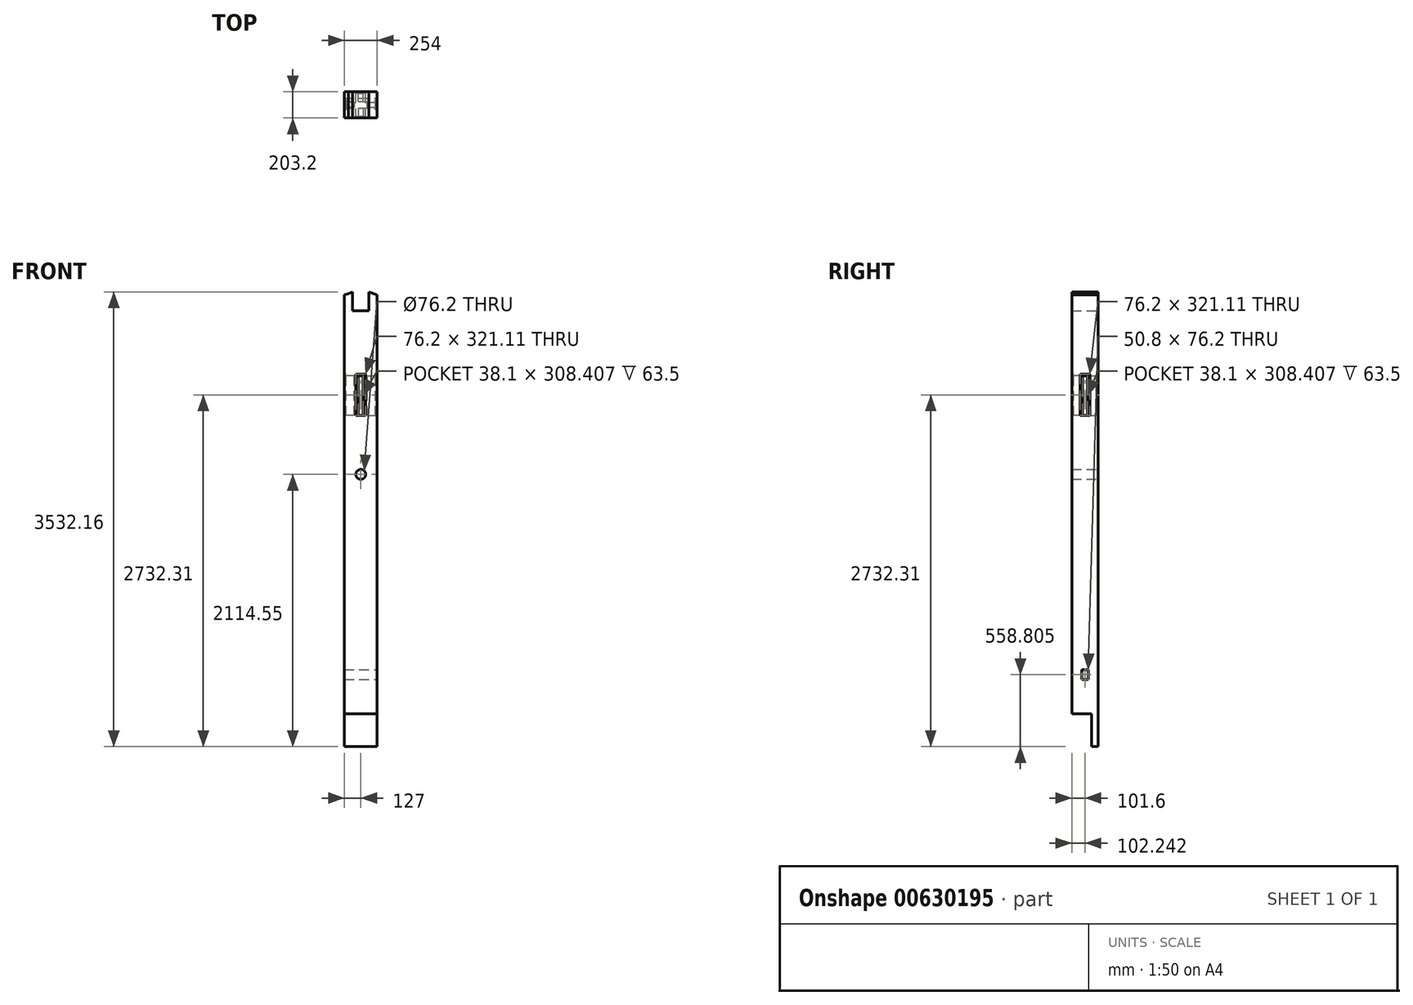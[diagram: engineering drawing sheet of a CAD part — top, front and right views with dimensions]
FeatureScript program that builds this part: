
annotation { "Feature Type Name" : "Feature", "Feature Type Description" : "" }
export const myFeature = defineFeature(function(context is Context, id is Id, definition is map)
    precondition{}
    {
        {
            var Q0;
            Q0=qCreatedBy(makeId("Front.planeOp"),FACE);
            var sketch = newSketch(context, id + "F0", { "sketchPlane" : qUnion([Q0])});
            skLineSegment(sketch, "E0.bottom", {"start": v(-127, 1679.58) * mm, "end": v(127, 1679.58) * mm});
            skLineSegment(sketch, "E0.top", {"start": v(-127, -1679.58) * mm, "end": v(127, -1679.58) * mm});
            skLineSegment(sketch, "E0.left", {"start": v(-127, 1679.58) * mm, "end": v(-127, -1679.58) * mm});
            skLineSegment(sketch, "E0.right", {"start": v(127, 1679.58) * mm, "end": v(127, -1679.57) * mm});
            skPoint(sketch, "E0.middle", {"position": v(0, 0) * mm});
            skLineSegment(sketch, "E1.bottom", {"start": v(-63.5, 1679.58) * mm, "end": v(63.5, 1679.58) * mm});
            skLineSegment(sketch, "E1.top", {"start": v(-63.5, 1450.98) * mm, "end": v(63.5, 1450.98) * mm});
            skLineSegment(sketch, "E1.left", {"start": v(-63.5, 1679.58) * mm, "end": v(-63.5, 1450.98) * mm});
            skLineSegment(sketch, "E1.right", {"start": v(63.5, 1679.58) * mm, "end": v(63.5, 1450.98) * mm});
            skPoint(sketch, "E1.middle", {"position": v(0, 1565.27) * mm});
            skLineSegment(sketch, "E2", {"start": v(-127, 1575.48) * mm, "end": v(-97.13, 1586.25) * mm});
            skLineSegment(sketch, "E3", {"start": v(-97.13, 1586.25) * mm, "end": v(-114.3, 1679.58) * mm});
            skLineSegment(sketch, "E4", {"start": v(-111.15, 1662.43) * mm, "end": v(-63.5, 1679.58) * mm});
            skLineSegment(sketch, "E5", {"start": v(127, 1575.96) * mm, "end": v(97.1, 1586.63) * mm});
            skLineSegment(sketch, "E6", {"start": v(97.1, 1586.63) * mm, "end": v(114.3, 1679.58) * mm});
            skLineSegment(sketch, "E7", {"start": v(111.16, 1662.6) * mm, "end": v(63.5, 1679.58) * mm});
            skLineSegment(sketch, "E8.bottom", {"start": v(-19.05, 946.58) * mm, "end": v(19.05, 946.58) * mm});
            skLineSegment(sketch, "E8.top", {"start": v(-19.05, 638.18) * mm, "end": v(19.05, 638.18) * mm});
            skLineSegment(sketch, "E8.left", {"start": v(-19.05, 946.58) * mm, "end": v(-19.05, 638.18) * mm});
            skLineSegment(sketch, "E8.right", {"start": v(19.05, 946.58) * mm, "end": v(19.05, 638.18) * mm});
            skPoint(sketch, "E8.middle", {"position": v(0, 792.38) * mm});
            skLineSegment(sketch, "E9.bottom", {"start": v(38.1, 638.18) * mm, "end": v(-38.1, 638.18) * mm});
            skLineSegment(sketch, "E9.top", {"start": v(38.1, 959.28) * mm, "end": v(-38.1, 959.28) * mm});
            skLineSegment(sketch, "E9.left", {"start": v(38.1, 638.18) * mm, "end": v(38.1, 959.28) * mm});
            skLineSegment(sketch, "E9.right", {"start": v(-38.1, 638.18) * mm, "end": v(-38.1, 959.28) * mm});
            skLineSegment(sketch, "E10", {"start": v(-127, 1575.48) * mm, "end": v(-63.5, 1598.5) * mm});
            skLineSegment(sketch, "E11", {"start": v(127, 1575.96) * mm, "end": v(63.5, 1598.58) * mm});
            skCircle(sketch, "E12", {"center": v(0, 180.97) * mm, "radius": 38.1 * mm});
            skSolve(sketch);
        }
        {
            var Q0;
            Q0=makeQuery(id+"F0.imprint","IMPRINT",FACE,{"disambiguationData":[TD([[makeQuery(id+"F0.imprint","IMPRINT",EDGE,{"derivedFrom":sQuery(id+"F0.wireOp",EDGE,"ph5wAFCl-OnS3-WXPz-KjN0-k0vqOy9yEcDQ.bottom")}),-1.0]])]});
            var Q1;
            Q1=makeQuery(id+"F0.imprint","IMPRINT",FACE,{"disambiguationData":[TD([[makeQuery(id+"F0.imprint","IMPRINT",EDGE,{"derivedFrom":sQuery(id+"F0.wireOp",EDGE,"E1.top")}),-1.0]])]});
            var Q2;
            Q2=makeQuery(id+"F0.imprint","IMPRINT",FACE,{"disambiguationData":[TD([[makeQuery(id+"F0.imprint","IMPRINT",EDGE,{"derivedFrom":sQuery(id+"F0.wireOp",EDGE,"E8.bottom")}),-1.0]])]});
            var Q3;
            Q3=makeQuery(id+"F0.imprint","IMPRINT",FACE,{"disambiguationData":[TD([[makeQuery(id+"F0.imprint","IMPRINT",EDGE,{"derivedFrom":sQuery(id+"F0.wireOp",EDGE,"E8.bottom")}),1.0]])]});
            extrude(context, id + "F1", {"entities" : qUnion([Q0, Q1, Q2, Q3]), "depth" : 203.2 * mm, "offsetDistance" : 25.4 * mm});
        }
        {
            var Q0;
            Q0=makeQuery(id+"F0.imprint","IMPRINT",FACE,{"disambiguationData":[TD([[makeQuery(id+"F0.imprint","IMPRINT",EDGE,{"derivedFrom":sQuery(id+"F0.wireOp",EDGE,"E8.bottom")}),-1.0]])]});
            extrude(context, id + "F2", {"entities" : qUnion([Q0]), "operationType" : NewBodyOperationType.REMOVE, "depth" : 76.2 * mm, "offsetDistance" : 25.4 * mm});
        }
        {
            var Q0;
            Q0=makeQuery(id+"F1.opExtrude","CAP_FACE",FACE,{"disambiguationData":[OSD([sQuery(id+"F0.wireOp",EDGE,"E0.left"),sQuery(id+"F0.wireOp",EDGE,"E0.right"),sQuery(id+"F0.wireOp",EDGE,"E1.top"),sQuery(id+"F0.wireOp",EDGE,"E1.left"),sQuery(id+"F0.wireOp",EDGE,"E1.right"),sQuery(id+"F0.wireOp",EDGE,"E0.top"),sQuery(id+"F0.wireOp",EDGE,"ph5wAFCl-OnS3-WXPz-KjN0-k0vqOy9yEcDQ.top"),sQuery(id+"F0.wireOp",EDGE,"ph5wAFCl-OnS3-WXPz-KjN0-k0vqOy9yEcDQ.left"),sQuery(id+"F0.wireOp",EDGE,"ph5wAFCl-OnS3-WXPz-KjN0-k0vqOy9yEcDQ.right"),sQuery(id+"F0.wireOp",EDGE,"E2"),sQuery(id+"F0.wireOp",EDGE,"E3"),sQuery(id+"F0.wireOp",EDGE,"E4"),sQuery(id+"F0.wireOp",EDGE,"E5"),sQuery(id+"F0.wireOp",EDGE,"E6"),sQuery(id+"F0.wireOp",EDGE,"E7")])],"isStart":false});
            var sketch = newSketch(context, id + "F3", { "sketchPlane" : qUnion([Q0])});
            skLineSegment(sketch, "E13.bottom", {"start": v(-19.05, 638.18) * mm, "end": v(19.05, 638.18) * mm});
            skLineSegment(sketch, "E13.top", {"start": v(-19.05, 946.58) * mm, "end": v(19.05, 946.58) * mm});
            skLineSegment(sketch, "E13.left", {"start": v(-19.05, 638.18) * mm, "end": v(-19.05, 946.58) * mm});
            skLineSegment(sketch, "E13.right", {"start": v(19.05, 638.18) * mm, "end": v(19.05, 946.58) * mm});
            skPoint(sketch, "E13.middle", {"position": v(0, 792.38) * mm});
            skLineSegment(sketch, "E14.bottom", {"start": v(-38.1, 638.18) * mm, "end": v(38.1, 638.18) * mm});
            skLineSegment(sketch, "E14.top", {"start": v(-38.1, 959.28) * mm, "end": v(38.1, 959.28) * mm});
            skLineSegment(sketch, "E14.left", {"start": v(-38.1, 638.18) * mm, "end": v(-38.1, 959.28) * mm});
            skLineSegment(sketch, "E14.right", {"start": v(38.1, 638.18) * mm, "end": v(38.1, 959.28) * mm});
            skSolve(sketch);
        }
        {
            var Q0;
            Q0=makeQuery(id+"F3.imprint","IMPRINT",FACE,{"disambiguationData":[TD([[makeQuery(id+"F3.imprint","IMPRINT",EDGE,{"derivedFrom":sQuery(id+"F3.wireOp",EDGE,"E13.top")}),-1.0]])]});
            extrude(context, id + "F4", {"entities" : qUnion([Q0]), "operationType" : NewBodyOperationType.REMOVE, "oppositeDirection" : true, "depth" : 76.2 * mm, "offsetDistance" : 25.4 * mm});
        }
        {
            var Q0;
            Q0=makeQuery(id+"F3.imprint","IMPRINT",FACE,{"disambiguationData":[TD([[makeQuery(id+"F3.imprint","IMPRINT",EDGE,{"derivedFrom":sQuery(id+"F3.wireOp",EDGE,"E13.top")}),1.0]])]});
            extrude(context, id + "F5", {"entities" : qUnion([Q0]), "operationType" : NewBodyOperationType.REMOVE, "oppositeDirection" : true, "depth" : 12.7 * mm, "offsetDistance" : 25.4 * mm});
        }
        {
            var Q0;
            Q0=makeQuery(id+"F0.imprint","IMPRINT",FACE,{"disambiguationData":[TD([[makeQuery(id+"F0.imprint","IMPRINT",EDGE,{"derivedFrom":sQuery(id+"F0.wireOp",EDGE,"E8.bottom")}),1.0]])]});
            extrude(context, id + "F6", {"entities" : qUnion([Q0]), "operationType" : NewBodyOperationType.REMOVE, "depth" : 12.7 * mm, "offsetDistance" : 25.4 * mm});
        }
        {
            var Q0;
            Q0=makeQuery(id+"F1.opExtrude","SWEPT_FACE",FACE,{"disambiguationData":[OSD([sQuery(id+"F0.wireOp",EDGE,"E0.right")])]});
            var sketch = newSketch(context, id + "F7", { "sketchPlane" : qUnion([Q0])});
            skLineSegment(sketch, "E15.bottom", {"start": v(-120.65, 638.18) * mm, "end": v(-82.55, 638.18) * mm});
            skLineSegment(sketch, "E15.top", {"start": v(-120.65, 946.58) * mm, "end": v(-82.55, 946.58) * mm});
            skLineSegment(sketch, "E15.left", {"start": v(-120.65, 638.18) * mm, "end": v(-120.65, 946.58) * mm});
            skLineSegment(sketch, "E15.right", {"start": v(-82.55, 638.18) * mm, "end": v(-82.55, 946.58) * mm});
            skPoint(sketch, "E15.middle", {"position": v(-101.6, 792.38) * mm});
            skLineSegment(sketch, "E16.bottom", {"start": v(-139.7, 638.18) * mm, "end": v(-63.5, 638.18) * mm});
            skLineSegment(sketch, "E16.top", {"start": v(-139.7, 959.28) * mm, "end": v(-63.5, 959.28) * mm});
            skLineSegment(sketch, "E16.left", {"start": v(-139.7, 638.18) * mm, "end": v(-139.7, 959.28) * mm});
            skLineSegment(sketch, "E16.right", {"start": v(-63.5, 638.18) * mm, "end": v(-63.5, 959.28) * mm});
            skLineSegment(sketch, "E17.bottom", {"start": v(-126.36, -1336.67) * mm, "end": v(-75.56, -1336.67) * mm});
            skLineSegment(sketch, "E17.top", {"start": v(-126.36, -1412.87) * mm, "end": v(-75.56, -1412.87) * mm});
            skLineSegment(sketch, "E17.left", {"start": v(-126.36, -1336.67) * mm, "end": v(-126.36, -1412.87) * mm});
            skLineSegment(sketch, "E17.right", {"start": v(-75.56, -1336.67) * mm, "end": v(-75.56, -1412.87) * mm});
            skPoint(sketch, "E17.middle", {"position": v(-100.96, -1374.77) * mm});
            skSolve(sketch);
        }
        {
            var Q0;
            Q0=makeQuery(id+"F7.imprint","IMPRINT",FACE,{"disambiguationData":[TD([[makeQuery(id+"F7.imprint","IMPRINT",EDGE,{"derivedFrom":sQuery(id+"F7.wireOp",EDGE,"E15.top")}),-1.0]])]});
            extrude(context, id + "F8", {"entities" : qUnion([Q0]), "operationType" : NewBodyOperationType.REMOVE, "oppositeDirection" : true, "depth" : 76.2 * mm, "offsetDistance" : 25.4 * mm});
        }
        {
            var Q0;
            Q0=makeQuery(id+"F7.imprint","IMPRINT",FACE,{"disambiguationData":[TD([[makeQuery(id+"F7.imprint","IMPRINT",EDGE,{"derivedFrom":sQuery(id+"F7.wireOp",EDGE,"E15.top")}),1.0]])]});
            extrude(context, id + "F9", {"entities" : qUnion([Q0]), "operationType" : NewBodyOperationType.REMOVE, "oppositeDirection" : true, "depth" : 12.7 * mm, "offsetDistance" : 25.4 * mm});
        }
        {
            var Q0;
            Q0=makeQuery(id+"F1.opExtrude","SWEPT_FACE",FACE,{"disambiguationData":[OSD([sQuery(id+"F0.wireOp",EDGE,"E0.left")])]});
            var sketch = newSketch(context, id + "F10", { "sketchPlane" : qUnion([Q0])});
            skLineSegment(sketch, "E18.bottom", {"start": v(82.55, 638.18) * mm, "end": v(120.65, 638.18) * mm});
            skLineSegment(sketch, "E18.top", {"start": v(82.55, 946.58) * mm, "end": v(120.65, 946.58) * mm});
            skLineSegment(sketch, "E18.left", {"start": v(82.55, 638.18) * mm, "end": v(82.55, 946.58) * mm});
            skLineSegment(sketch, "E18.right", {"start": v(120.65, 638.18) * mm, "end": v(120.65, 946.58) * mm});
            skPoint(sketch, "E18.middle", {"position": v(101.6, 792.38) * mm});
            skLineSegment(sketch, "E19.bottom", {"start": v(63.5, 638.18) * mm, "end": v(139.7, 638.18) * mm});
            skLineSegment(sketch, "E19.top", {"start": v(63.5, 959.28) * mm, "end": v(139.7, 959.28) * mm});
            skLineSegment(sketch, "E19.left", {"start": v(63.5, 638.18) * mm, "end": v(63.5, 959.28) * mm});
            skLineSegment(sketch, "E19.right", {"start": v(139.7, 638.18) * mm, "end": v(139.7, 959.28) * mm});
            skSolve(sketch);
        }
        {
            var Q0;
            Q0=makeQuery(id+"F10.imprint","IMPRINT",FACE,{"disambiguationData":[TD([[makeQuery(id+"F10.imprint","IMPRINT",EDGE,{"derivedFrom":sQuery(id+"F10.wireOp",EDGE,"E18.top")}),-1.0]])]});
            extrude(context, id + "F11", {"entities" : qUnion([Q0]), "operationType" : NewBodyOperationType.REMOVE, "oppositeDirection" : true, "depth" : 76.2 * mm, "offsetDistance" : 25.4 * mm});
        }
        {
            var Q0;
            Q0=makeQuery(id+"F10.imprint","IMPRINT",FACE,{"disambiguationData":[TD([[makeQuery(id+"F10.imprint","IMPRINT",EDGE,{"derivedFrom":sQuery(id+"F10.wireOp",EDGE,"E18.top")}),1.0]])]});
            extrude(context, id + "F12", {"entities" : qUnion([Q0]), "operationType" : NewBodyOperationType.REMOVE, "oppositeDirection" : true, "depth" : 12.7 * mm, "offsetDistance" : 25.4 * mm});
        }
        {
            var Q0;
            Q0=makeQuery(id+"F7.imprint","IMPRINT",FACE,{"disambiguationData":[TD([[makeQuery(id+"F7.imprint","IMPRINT",EDGE,{"derivedFrom":sQuery(id+"F7.wireOp",EDGE,"E17.bottom")}),-1.0]])]});
            extrude(context, id + "F13", {"entities" : qUnion([Q0]), "operationType" : NewBodyOperationType.REMOVE, "oppositeDirection" : true, "depth" : 254 * mm, "offsetDistance" : 25.4 * mm});
        }
        {
            var Q0;
            Q0=makeQuery(id+"F1.opExtrude","SWEPT_FACE",FACE,{"disambiguationData":[OSD([sQuery(id+"F0.wireOp",EDGE,"E0.top")])]});
            var sketch = newSketch(context, id + "F14", { "sketchPlane" : qUnion([Q0])});
            skLineSegment(sketch, "E20.bottom", {"start": v(-127, 0) * mm, "end": v(127, 0) * mm});
            skLineSegment(sketch, "E20.top", {"start": v(-127, 50.8) * mm, "end": v(127, 50.8) * mm});
            skLineSegment(sketch, "E20.left", {"start": v(-127, 0) * mm, "end": v(-127, 50.8) * mm});
            skLineSegment(sketch, "E20.right", {"start": v(127, 0) * mm, "end": v(127, 50.8) * mm});
            skSolve(sketch);
        }
        {
            var Q0;
            Q0 = qSketchRegion(id + "F14", true);
            extrude(context, id + "F15", {"entities" : qUnion([Q0]), "operationType" : NewBodyOperationType.ADD, "depth" : 254 * mm, "offsetDistance" : 25.4 * mm});
        }
    });
